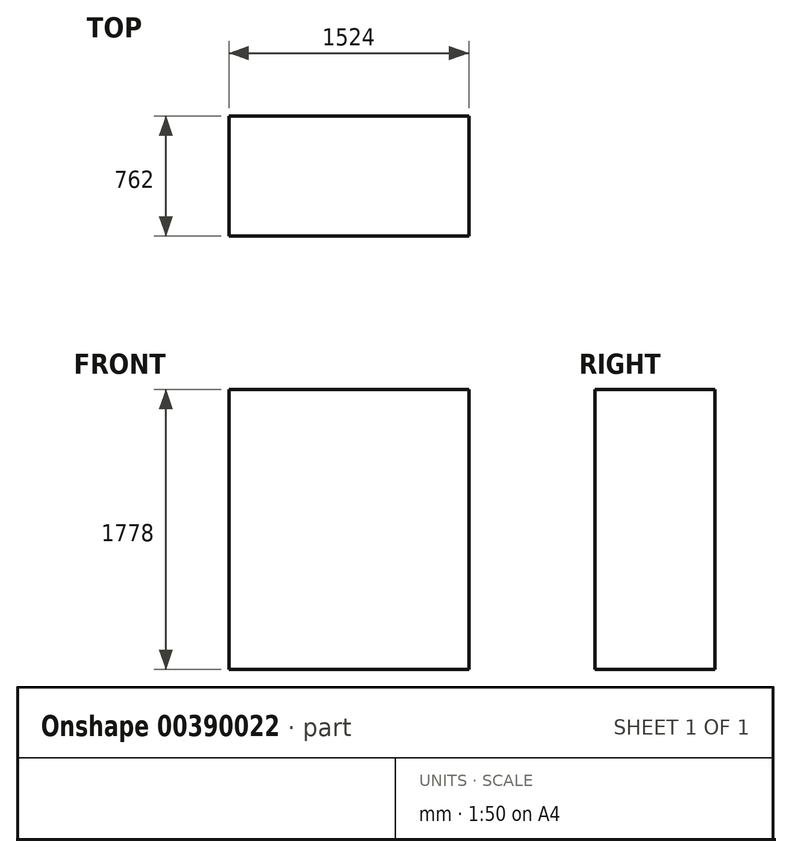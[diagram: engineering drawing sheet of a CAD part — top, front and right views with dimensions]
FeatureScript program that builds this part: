
annotation { "Feature Type Name" : "Feature", "Feature Type Description" : "" }
export const myFeature = defineFeature(function(context is Context, id is Id, definition is map)
    precondition{}
    {
        {
            var Q0;
            Q0=qCreatedBy(makeId("Front.planeOp"),FACE);
            var sketch = newSketch(context, id + "F0", { "sketchPlane" : qUnion([Q0])});
            skLineSegment(sketch, "E0.bottom", {"start": v(762, 889) * mm, "end": v(-762, 889) * mm});
            skLineSegment(sketch, "E0.top", {"start": v(762, -889) * mm, "end": v(-762, -889) * mm});
            skLineSegment(sketch, "E0.left", {"start": v(762, 889) * mm, "end": v(762, -889) * mm});
            skLineSegment(sketch, "E0.right", {"start": v(-762, 889) * mm, "end": v(-762, -889) * mm});
            skPoint(sketch, "E0.middle", {"position": v(0, 0) * mm});
            skSolve(sketch);
        }
        {
            var Q0;
            Q0 = qSketchRegion(id + "F0", true);
            extrude(context, id + "F1", {"entities" : qUnion([Q0]), "depth" : 762 * mm});
        }
    });
